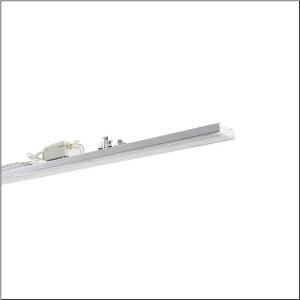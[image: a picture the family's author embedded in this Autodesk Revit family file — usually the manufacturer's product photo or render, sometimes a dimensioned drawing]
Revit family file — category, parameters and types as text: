
# Revit family: licross_r__21_recessed_mo_52te107n485g_2b82
name_source: partatom
category: Lighting Fixtures
units: mm (PartAtom-declared; Revit-internal decimal feet)

## family parameters
Cut with Voids When Loaded = No
Host = Face
Light Source = No
Part Type = Normal
Room Calculation Point = No
Round Connector Dimension = Use Diameter
Shared = No

## types (1)
- Licross® 21 Recessed MO (1 x LED, 8580 lm, 47.9 W, 4000K)
    Apparent Load = 48 VA
    CIE Flux Codes = 50 81 96 100 100
    Color Rendering = 80
    Color Temperature = 4000K
    Default Elevation = 1800 mm
    Description = Licross® 21 Recessed MO, luminaire insert, of sheet steel, galvanised, coil coated, white, length: 1.500mm, width: 66mm, height: 67mm, LED rated luminous flux: 8.560lm, light colour: 840, control gear: ON/OFF, with plug, 3-pole, with phase selection, mains connection: 220..240V, AC, 50/60Hz, rated input power: 48W, halogen-free wiring, primary optical cover: cover, of PMMA, light emission: direct distribution, primary light characteristic: symmetric, protection rating (complete): IP54, insulation class (complete): insulation class I (protective earthing), certification: CE, ENEC, VDE, UKCA, protection symbol: D if used in an environment with non-conductive dust loads with corresponding accessories, impact resistance: IK06, permissible ambient temperature for indoor applications: -35..+40°C, corresponds to IFS (International Featured Standards) requirements for safety and quality in the food industry, reducing of maximum allowable ambient temperature of 5°C with ceiling mounting, LABS conformity tested according to VDMA 24364:2018-05, packaging unit: 1 piece
    Height = 58 mm
    Lamp = 1 x LED
    Lamp Light Flux = 8580 lm
    Lamp Power = 47.9 W
    Lamp count = 1
    Length = 1500 mm
    Luminous efficacy = 179 lm/W
    Manufacturer = Siteco
    ModVariant = No
    Model = 52TE107N485G
    Mounting Place = Ceiling
    Mounting Type = Pendant
    Number of Poles = 1
    OnlyDefault = Yes
    Power Factor = 1
    Product Name = Licross® 21 Recessed MO
    Product group = luminaire insert
    ProductGroupID = 901
    Protection Class = Protection class I
    Protection Degree = IP 54
    RLX_Detail_Level = 1
    RLX_Emergency_Light_Flux = 0 lm
    RLX_Emergency_Type = 0
    RLX_Emergency_Type_DB = No
    RlxData = <blob elided: 20761 chars, md5=be73d292>
    Socket = socket
    Standby Power = 0 W
    System Light Flux = 8580 lm
    System Power = 48 W
    Type Comments = Product without accessories
    Type Image = l_1296930.jpg
    URL = http://relux.com
    VarID = ---
    Voltage = 0 V
    Weight = 0.00 kg
    Width = 66 mm

## geometry (parser evidence)
native form markers: Blend x4, Sweep x11
no freeform markers — native parametric forms only
